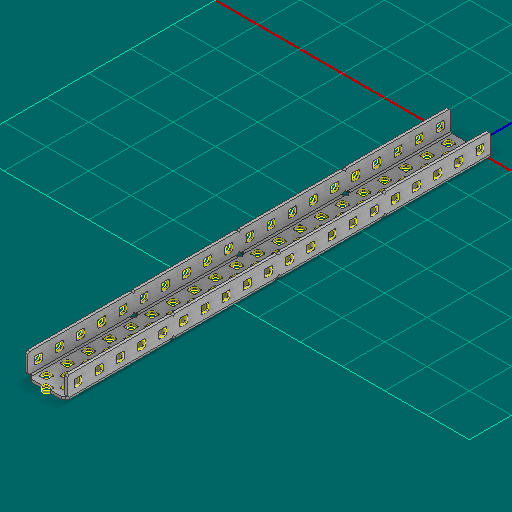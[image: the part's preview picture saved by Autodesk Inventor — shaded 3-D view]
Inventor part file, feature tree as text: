
AUTODESK INVENTOR PART (.ipt)
format: ipt  version: 2025 (Build 290162000, 162)  size: 1,710,592 bytes
history: native  units: in
note: dims shown in document units (in); Inventor stores cm internally (conversion verified against a paired STEP export)
features: other x206, sketch x5, sheet_metal_op x1
ambient origin geometry x8: Origin, YZ Plane, XZ Plane, XY Plane, X Axis, Y Axis, Z Axis, Center Point
bodies: Solid1 (feature_tree)
feature tree (212):
  other  "Alu C 1x2x1x20.ipt"
  other  "Solid1::Alu C 1x2x1x20.ipt"
  other  "TaggingFeature1"
  sketch  "Sketch1"  dims[d0=0.3937in]
  sketch  "Sketch2"  dims[d1=0.0625in]
  sketch  "Sketch3"
  other  "Flange Pattern Sketch"
  sketch  "Sketch9"
  sheet_metal_op  "Body Pattern Sketch"
  other  "Arc Length"
  sketch  "Sketch14"
  other  "Flange Pattern Plane"
  other  "Srf1"
  other  "Srf2"
  other  "Srf3"
  other  "Srf4"
  other  "Srf5"
  other  "Srf6"
  other  "Srf7"
  other  "Srf8"
  other  "Srf9"
  other  "Srf10"
  other  "Srf11"
  other  "Srf12"
  other  "Srf13"
  other  "Srf14"
  other  "Srf15"
  other  "Srf16"
  other  "Srf17"
  other  "Srf18"
  other  "Srf19"
  other  "Srf20"
  other  "Srf21"
  other  "Srf22"
  other  "Srf23"
  other  "Srf24"
  other  "Srf25"
  other  "Srf26"
  other  "Srf27"
  other  "Srf28"
  other  "Srf29"
  other  "Srf30"
  other  "Srf31"
  other  "Srf32"
  other  "Srf33"
  other  "Srf34"
  other  "Srf35"
  other  "Srf36"
  other  "Srf37"
  other  "Srf38"
  other  "Srf39"
  other  "Srf40"
  other  "Srf41"
  other  "Srf42"
  other  "Srf43"
  other  "Srf44"
  other  "Srf45"
  other  "Srf46"
  other  "Srf47"
  other  "Srf48"
  other  "Srf49"
  other  "Srf50"
  other  "Srf51"
  other  "Srf52"
  other  "Srf53"
  other  "Srf54"
  other  "Srf55"
  other  "Srf56"
  other  "Srf57"
  other  "Srf58"
  other  "Srf59"
  other  "Srf60"
  other  "Srf61"
  other  "Srf62"
  other  "Srf63"
  other  "Srf64"
  other  "Srf65"
  other  "Srf66"
  other  "Srf67"
  other  "Srf68"
  other  "Srf69"
  other  "Srf70"
  other  "Srf71"
  other  "Srf72"
  other  "Srf73"
  other  "Srf74"
  other  "Srf75"
  other  "Srf76"
  other  "Srf77"
  other  "Srf78"
  other  "Srf79"
  other  "Srf80"
  other  "Srf81"
  other  "Srf82"
  other  "Srf83"
  other  "Srf84"
  other  "Srf85"
  other  "Srf86"
  other  "Srf87"
  other  "Srf88"
  other  "Srf89"
  other  "Srf90"
  other  "Srf91"
  other  "Srf92"
  other  "Srf93"
  other  "Srf94"
  other  "Srf95"
  other  "Srf96"
  other  "Srf97"
  other  "Srf98"
  other  "Srf99"
  other  "Srf100"
  other  "Srf1::Derived"
  other  "Srf2::Derived"
  other  "Srf823::Derived"
  other  "Srf824::Derived"
  other  "Srf825::Derived"
  other  "Srf826::Derived"
  other  "Srf827::Derived"
  other  "Srf828::Derived"
  other  "Srf829::Derived"
  other  "Srf922::Derived"
  other  "Srf923::Derived"
  other  "Srf924::Derived"
  other  "Srf925::Derived"
  other  "Srf926::Derived"
  other  "Srf1143::Derived"
  other  "Srf1144::Derived"
  other  "Srf1145::Derived"
  other  "Srf1146::Derived"
  other  "Srf1147::Derived"
  other  "Srf1148::Derived"
  other  "Srf1149::Derived"
  other  "Srf1150::Derived"
  other  "Srf1151::Derived"
  other  "Srf1152::Derived"
  other  "Srf1153::Derived"
  other  "Srf1154::Derived"
  other  "Srf1155::Derived"
  other  "Srf1156::Derived"
  other  "Srf1157::Derived"
  other  "Srf1158::Derived"
  other  "Srf1159::Derived"
  other  "Srf1160::Derived"
  other  "Srf1161::Derived"
  other  "Srf1162::Derived"
  other  "Srf1163::Derived"
  other  "Srf1164::Derived"
  other  "Srf1165::Derived"
  other  "Srf1166::Derived"
  other  "Srf1167::Derived"
  other  "Srf1168::Derived"
  other  "Srf91::Derived"
  other  "Srf92::Derived"
  other  "Srf856::Derived"
  other  "Srf857::Derived"
  other  "Srf858::Derived"
  other  "Srf859::Derived"
  other  "Srf860::Derived"
  other  "Srf861::Derived"
  other  "Srf862::Derived"
  other  "Srf959::Derived"
  other  "Srf960::Derived"
  other  "Srf961::Derived"
  other  "Srf962::Derived"
  other  "Srf963::Derived"
  other  "Srf1199::Derived"
  other  "Srf1200::Derived"
  other  "Srf1201::Derived"
  other  "Srf1202::Derived"
  other  "Srf1203::Derived"
  other  "Srf1204::Derived"
  other  "Srf1205::Derived"
  other  "Srf1206::Derived"
  other  "Srf1207::Derived"
  other  "Srf1208::Derived"
  other  "Srf1209::Derived"
  other  "Srf1210::Derived"
  other  "Srf1211::Derived"
  other  "Srf1212::Derived"
  other  "Srf1213::Derived"
  other  "Srf1214::Derived"
  other  "Srf1215::Derived"
  other  "Srf1216::Derived"
  other  "Srf1217::Derived"
  other  "Srf1218::Derived"
  other  "Srf1219::Derived"
  other  "Srf1220::Derived"
  other  "Srf1221::Derived"
  other  "Srf1222::Derived"
  other  "Srf1223::Derived"
  other  "Srf1224::Derived"
  other  "Srf786::Derived"
  other  "Srf889::Derived"
  other  "Srf890::Derived"
  other  "Srf891::Derived"
  other  "Srf892::Derived"
  other  "Srf893::Derived"
  other  "Srf894::Derived"
  other  "Srf895::Derived"
  other  "Srf896::Derived"
  other  "Srf996::Derived"
  other  "Srf997::Derived"
  other  "Srf998::Derived"
  other  "Srf999::Derived"
  other  "Srf1000::Derived"
  other  "Srf1255::Derived"
  other  "Srf1256::Derived"
  other  "Srf1257::Derived"
  other  "Srf1258::Derived"
  other  "Srf1259::Derived"
  other  "Srf1260::Derived"
